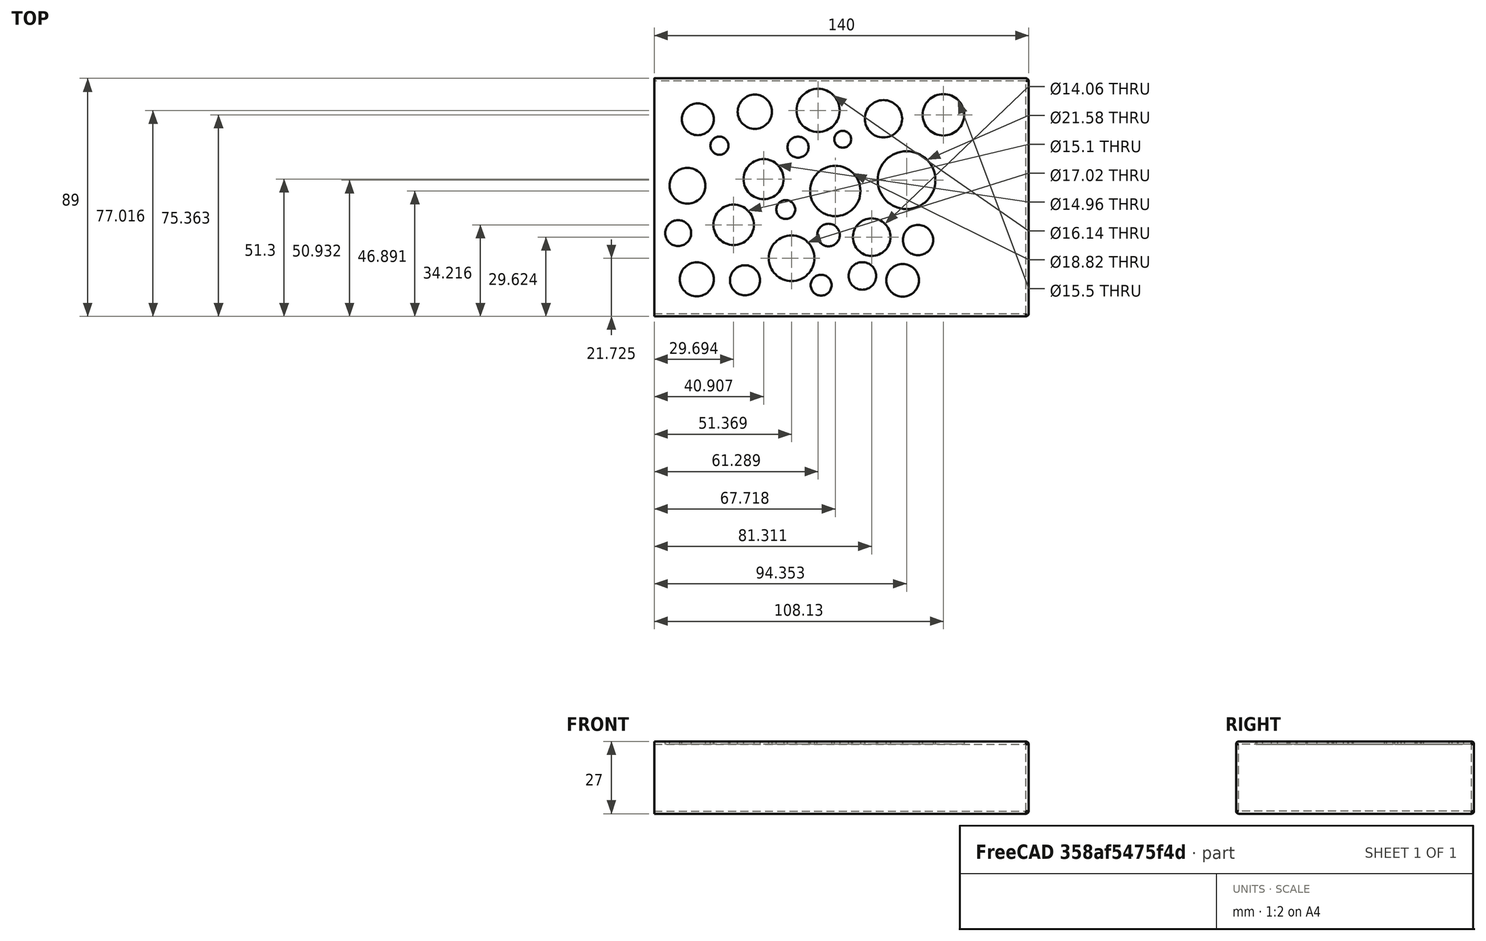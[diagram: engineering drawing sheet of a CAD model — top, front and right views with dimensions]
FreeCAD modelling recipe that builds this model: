
FCSTD DOCUMENT  (FreeCAD 0.18R4 (GitTag))
Label: Biocube 29 Filter Holder
License: All rights reserved
LicenseURL: http://en.wikipedia.org/wiki/All_rights_reserved
objects: Sketcher::SketchObject×2, PartDesign::Pad×1, PartDesign::Thickness×1, PartDesign::Pocket×1, PartDesign::Body×1
note: 8 computed .brp shape members not serialized (recipe doc carries the construction recipe); baked Part::Feature solids carry a one-line shape summary decoded from their .brp

FEATURE [Sketcher::SketchObject] Sketch001
  MapMode = 5
  sketch-geometry (4):
    g0: LineSegment StartX=-98.6361 StartY=-57.4943 StartZ=0 EndX=40.3639 EndY=-57.4943 EndZ=0
    g1: LineSegment StartX=40.3639 StartY=-57.4943 StartZ=0 EndX=40.3639 EndY=29.5057 EndZ=0
    g2: LineSegment StartX=40.3639 StartY=29.5057 StartZ=0 EndX=-98.6361 EndY=29.5057 EndZ=0
    g3: LineSegment StartX=-98.6361 StartY=29.5057 StartZ=0 EndX=-98.6361 EndY=-57.4943 EndZ=0
  constraints (10):
    c: Coincident(g0,g1)
    c: Coincident(g1,g2)
    c: Coincident(g2,g3)
    c: Coincident(g3,g0)
    c: Horizontal(g0)
    c: Horizontal(g2)
    c: Vertical(g1)
    c: Vertical(g3)
    c: DistanceY(g0,g1) = 87
    c: DistanceX(g2,g1) = 139
FEATURE [PartDesign::Pad] Pad
  Length = 25
  Length2 = 100
  Profile = -> Sketch001
  Type = 0
FEATURE [PartDesign::Thickness] Thickness
  Base = -> Pad [Face4]
  BaseFeature = -> Pad
  Join = 0
  Mode = 0
  Value = 1
FEATURE [Sketcher::SketchObject] Sketch002
  MapMode = 5
  Placement = pos=(0,0,26) rot=(0,0,1;0rad)
  Support = -> [Thickness]
  sketch-geometry (24):
    g0: Circle CenterX=-82.3346 CenterY=15.2163 CenterZ=0 NormalX=0 NormalY=0 NormalZ=1 AngleXU=0 Radius=5.94705
    g1: Circle CenterX=-61.0213 CenterY=18.0212 CenterZ=0 NormalX=0 NormalY=0 NormalZ=1 AngleXU=0 Radius=6.39154
    g2: Circle CenterX=-57.7329 CenterY=-7.18999 CenterZ=0 NormalX=0 NormalY=0 NormalZ=1 AngleXU=0 Radius=7.47971
    g3: Circle CenterX=-86.2325 CenterY=-9.65631 CenterZ=0 NormalX=0 NormalY=0 NormalZ=1 AngleXU=0 Radius=6.69004
    g4: Circle CenterX=-68.9463 CenterY=-24.274 CenterZ=0 NormalX=0 NormalY=0 NormalZ=1 AngleXU=0 Radius=7.55147
    g5: Circle CenterX=-82.7231 CenterY=-44.6637 CenterZ=0 NormalX=0 NormalY=0 NormalZ=1 AngleXU=0 Radius=6.34199
    g6: Circle CenterX=-47.2707 CenterY=-36.765 CenterZ=0 NormalX=0 NormalY=0 NormalZ=1 AngleXU=0 Radius=8.50949
    g7: Circle CenterX=-30.9222 CenterY=-11.5993 CenterZ=0 NormalX=0 NormalY=0 NormalZ=1 AngleXU=0 Radius=9.40958
    g8: Circle CenterX=-37.3514 CenterY=18.526 CenterZ=0 NormalX=0 NormalY=0 NormalZ=1 AngleXU=0 Radius=8.06988
    g9: Circle CenterX=-17.3291 CenterY=-28.8663 CenterZ=0 NormalX=0 NormalY=0 NormalZ=1 AngleXU=0 Radius=7.03083
    g10: Circle CenterX=-20.8192 CenterY=-43.3779 CenterZ=0 NormalX=0 NormalY=0 NormalZ=1 AngleXU=0 Radius=5.14662
    g11: Circle CenterX=-12.9205 CenterY=15.4033 CenterZ=0 NormalX=0 NormalY=0 NormalZ=1 AngleXU=0 Radius=6.98267
    g12: Circle CenterX=9.48984 CenterY=16.8728 CenterZ=0 NormalX=0 NormalY=0 NormalZ=1 AngleXU=0 Radius=7.75212
    g13: Circle CenterX=-4.28699 CenterY=-7.55813 CenterZ=0 NormalX=0 NormalY=0 NormalZ=1 AngleXU=0 Radius=10.7878
    g14: Circle CenterX=0 CenterY=-29.9684 CenterZ=0 NormalX=0 NormalY=0 NormalZ=1 AngleXU=0 Radius=5.65876
    g15: Circle CenterX=-44.8587 CenterY=4.77725 CenterZ=0 NormalX=0 NormalY=0 NormalZ=1 AngleXU=0 Radius=3.93116
    g16: Circle CenterX=-74.2492 CenterY=5.32832 CenterZ=0 NormalX=0 NormalY=0 NormalZ=1 AngleXU=0 Radius=3.37712
    g17: Circle CenterX=-64.6973 CenterY=-45.003 CenterZ=0 NormalX=0 NormalY=0 NormalZ=1 AngleXU=0 Radius=5.62287
    g18: Circle CenterX=-36.2252 CenterY=-46.84 CenterZ=0 NormalX=0 NormalY=0 NormalZ=1 AngleXU=0 Radius=3.90532
    g19: Circle CenterX=-33.4698 CenterY=-28.1035 CenterZ=0 NormalX=0 NormalY=0 NormalZ=1 AngleXU=0 Radius=4.22889
    g20: Circle CenterX=-49.4509 CenterY=-18.5515 CenterZ=0 NormalX=0 NormalY=0 NormalZ=1 AngleXU=0 Radius=3.52859
    g21: Circle CenterX=-28.1428 CenterY=7.71631 CenterZ=0 NormalX=0 NormalY=0 NormalZ=1 AngleXU=0 Radius=3.16034
    g22: Circle CenterX=-5.73246 CenterY=-45.003 CenterZ=0 NormalX=0 NormalY=0 NormalZ=1 AngleXU=0 Radius=6.10618
    g23: Circle CenterX=-89.6793 CenterY=-27.3687 CenterZ=0 NormalX=0 NormalY=0 NormalZ=1 AngleXU=0 Radius=4.85306
  constraints (1):
    c: PointOnObject(g14,g-2)
FEATURE [PartDesign::Pocket] Pocket
  BaseFeature = -> Thickness
  Length = 5
  Length2 = 100
  Profile = -> Sketch002
  Type = 0
FEATURE [PartDesign::Body] Body001
  Group = -> [Sketch001,Pad,Thickness,Sketch002,Pocket]
  Origin = -> Origin001
  Tip = -> Pocket
